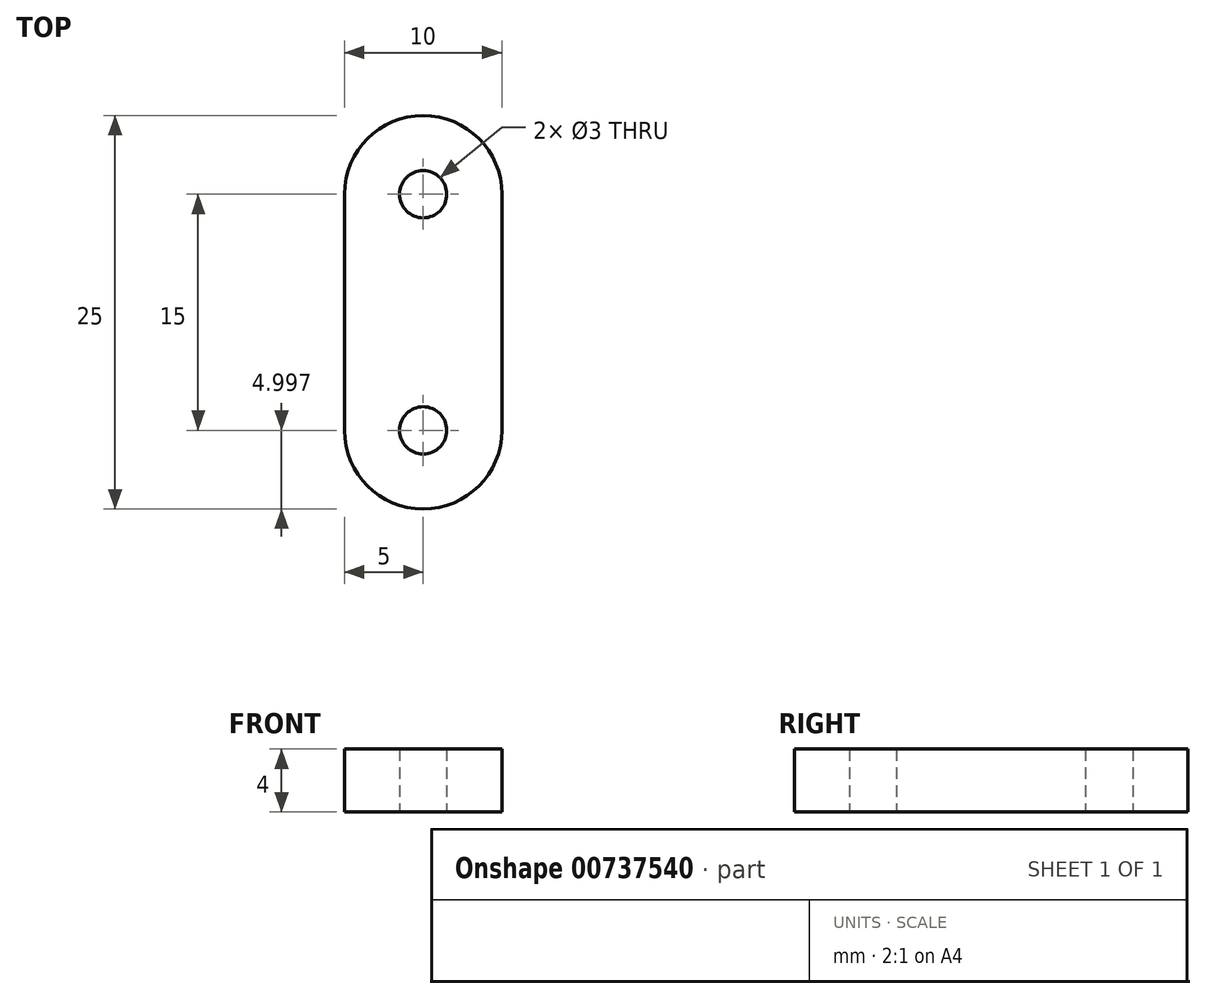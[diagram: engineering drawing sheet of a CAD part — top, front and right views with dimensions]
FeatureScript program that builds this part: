
annotation { "Feature Type Name" : "Feature", "Feature Type Description" : "" }
export const myFeature = defineFeature(function(context is Context, id is Id, definition is map)
    precondition{}
    {
        {
            var Q0;
            Q0=qCreatedBy(makeId("Top.planeOp"),FACE);
            var sketch = newSketch(context, id + "F0", { "sketchPlane" : qUnion([Q0])});
            skCircle(sketch, "E0", {"center": v(0, 6.82) * mm, "radius": 5 * mm});
            skCircle(sketch, "E1", {"center": v(0, -8.18) * mm, "radius": 5 * mm});
            skLineSegment(sketch, "E2", {"start": v(-5, 6.82) * mm, "end": v(-5, -8.18) * mm});
            skLineSegment(sketch, "E3", {"start": v(5, 6.82) * mm, "end": v(5, -8.18) * mm});
            skCircle(sketch, "E4", {"center": v(0, 6.82) * mm, "radius": 1.5 * mm});
            skCircle(sketch, "E5", {"center": v(0, -8.18) * mm, "radius": 1.5 * mm});
            skSolve(sketch);
        }
        {
            var Q0;
            Q0=makeQuery(id+"F0.imprint","IMPRINT",FACE,{"disambiguationData":[TD([[makeQuery(id+"F0.imprint","IMPRINT",EDGE,{"derivedFrom":sQuery(id+"F0.wireOp",EDGE,"E4")}),-1.0]])]});
            var Q1;
            {var subQ0=sQuery(id+"F0.wireOp",EDGE,"E2");Q1=makeQuery(id+"F0.imprint","IMPRINT",FACE,{"disambiguationData":[TD([[makeQuery(id+"F0.imprint","IMPRINT",EDGE,{"derivedFrom":subQ0}),1.0]])]});}
            var Q2;
            Q2=makeQuery(id+"F0.imprint","IMPRINT",FACE,{"disambiguationData":[TD([[makeQuery(id+"F0.imprint","IMPRINT",EDGE,{"derivedFrom":sQuery(id+"F0.wireOp",EDGE,"E5")}),-1.0]])]});
            extrude(context, id + "F1", {"entities" : qUnion([Q0, Q1, Q2]), "depth" : 4 * mm, "offsetDistance" : 25 * mm});
        }
    });
